# Revit family: 23799-Deca_Misturador de Parede_Pérola_1878-108
name_source: partatom
category: Plumbing Fixtures
units: mm (PartAtom-declared; Revit-internal decimal feet)

## family parameters
Cut with Voids When Loaded = No
Host = Face
Part Type = Normal
Room Calculation Point = No
Round Connector Dimension = Use Radius
Shared = No

## types (2) — shared parameters
Acompanha o Produto = BASE COM MECANISMO,CHAVE DO AREJADOR,CHAVE ALLEN
Aprovado por = quattroD
Atendimento ao Cliente = 0800 011 7073
Categoria = METAIS PARA BANHEIRO
Composição Anel Vedação = -
Composição Assento = -
Composição Básica = Liga de Cobre (bronze e latão),Plásticos de Engenharia,Elastômeros
Composição Componente = -
Consumo = -
Cor Interna = -
Cor Secundária = -
Cores Componente = -
Criado por = quattroD
Código Pai = 1878.C108.MT
Default Elevation = 1.1 m
Description = MIST LAV PAREDE DN/20 PEROLA-SM MT
Diâmetro Água Fria = 0.02 m
Informações Complementares = -
Itens de Instalação = CHAVE ALLEN
Linha = Pérola
Manufacturer = Deca
Norma = NBR 16749
Peso Líquido (Kg) = 2.595
Pressão mín. Aquec. Acúmulo = -
Pressão mín. Aquec. Passagem = -
Raio Água Fria = 0.01 m
Saída de Esgoto = -
Segmento = -
Tipo de dispositivo economizador = DECA COMFORT
Tipo de mecanismo utilizado = MVC  - 1/4 de volta
Tipo de rosca de entrada = BSP NBR 8133
Tipo de rosca de saída = -
URL = www.deca.com.br
Vazão na Pressão máx. (L/min) = 6
Vazão na Pressão mín. (L/min) = 4
zero-valued in all types: CWFU, Diâmetro Ponto de Esgoto, Raio Ponto de Esgoto, WFU

## per-type parameters (varying)
| type | Cor Principal | Material | Model |
| 1878.C108.MT_CROMADO | Cromado Matte | Deca_Cromado | 1878.C108.MT |
| 1878.SM108.MT_SUMMER GOLD | Summer Gold | Deca_Summer Gold | 1878.SM108.MT |

## geometry (parser evidence)
native form markers: Sweep x2
no freeform markers — native parametric forms only
